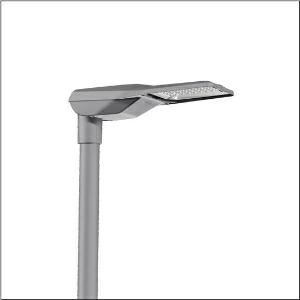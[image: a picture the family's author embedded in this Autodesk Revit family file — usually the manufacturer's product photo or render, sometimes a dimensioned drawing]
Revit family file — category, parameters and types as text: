
# Revit family: streetlight_sl_21_mini___st0_8a_5xe6c33a08hb_be66
name_source: partatom
category: Lighting Fixtures
units: mm (PartAtom-declared; Revit-internal decimal feet)

## family parameters
Cut with Voids When Loaded = No
Host = Face
Light Source = No
Part Type = Normal
Room Calculation Point = No
Round Connector Dimension = Use Diameter
Shared = No

## types (1)
- --- (1 x LED, 9040 lm, 66 W, 3000K)
    Apparent Load = 66 VA
    CIE Flux Codes = 38 75 97 100 100
    Color Rendering = 70
    Color Temperature = 3000K
    Default Elevation = 1800 mm
    Description = Streetlight SL 21 mini, mast luminaire, primary light control with lens, of PMMA, primary optical cover: cover, of toughened safety glass, transparent, light distribution: ST0.8a, light emission: direct distribution, primary light characteristic: asymmetric, installation type: post-top, side-entry, LED, 3G 1.5mm², High Power LED, rated luminous flux: 9.040lm, luminous efficacy: 137lm/W, light colour: 730, colour temperature: 3000K, control: overheat protection, constant luminous flux control, time-dependent luminous flux control, flexible luminous flux parameterisation, mains connection: 230..240V, AC, 50/60Hz, connection cable pre-assembled, cable length: 8,5m, wiring characteristics: H07RN-F, start of lifetime: 66W, end of service life: 69W, reduction: 30W, luminaire housing, of diecast aluminium, powder-coated, Siteco® metallic grey (DB 702S), corrosivity category C5 mid according to DIN EN ISO 12944, please order mast flange separately, inclination adjustable: 0°, 5°, 10°, 15°, sealing non-destructively replaceable, multi-level sealing system, length: 628mm, width: 235mm, height: 110mm, mast flange for spigot size: 42mm (side-entry): 5XC10008XM4, 60/48mm (side-entry/post-top): 5XC10108XM2, 76/60mm (side-entry/post-top): 5XC10108XM1, protection rating (complete): IP66, insulation class (complete): insulation class II (safety insulation), certification: CE, ENEC, ENEC+, VDE, impact resistance: IK09, permissible operating ambient temperature for outdoor applications: -40..+50°C, standard-compliant lighting for roads and squares, packaging unit: 1 piece

Light Distribution: ST0.8a
    Height = 110 mm
    Lamp = 1 x LED
    Lamp Light Flux = 9040 lm
    Lamp Power = 66 W
    Lamp count = 1
    Length = 625 mm
    Luminous efficacy = 137 lm/W
    Manufacturer = Siteco
    ModVariant = No
    Model = 5XE6C33A08HB
    Number of Poles = 1
    OnlyDefault = Yes
    Power Factor = 1
    Product Name = Streetlight SL 21 mini | ST0.8a
    Product group = mast luminaire | pylon top
    ProductGroupID = 6100
    Protection Class = Protection class II
    Protection Degree = IP 66
    RLX_Detail_Level = 1
    RLX_Emergency_Light_Flux = 0 lm
    RLX_Emergency_Type = 0
    RLX_Emergency_Type_DB = No
    RlxData = <blob elided: 91937 chars, md5=0bec984a>
    Socket = socket
    Standby Power = 0 W
    System Light Flux = 9040 lm
    System Power = 66 W
    Type Comments = factory setting: luminous flux: 100 % | Output Level: 100 % | 670 mA
    Type Image = l_1003519.jpg
    URL = http://relux.com
    VarID = @adj_118357
    Voltage = 0 V
    Weight = 0.00 kg
    Width = 234 mm

## geometry (parser evidence)
native form markers: Blend x4, Sweep x11
no freeform markers — native parametric forms only
